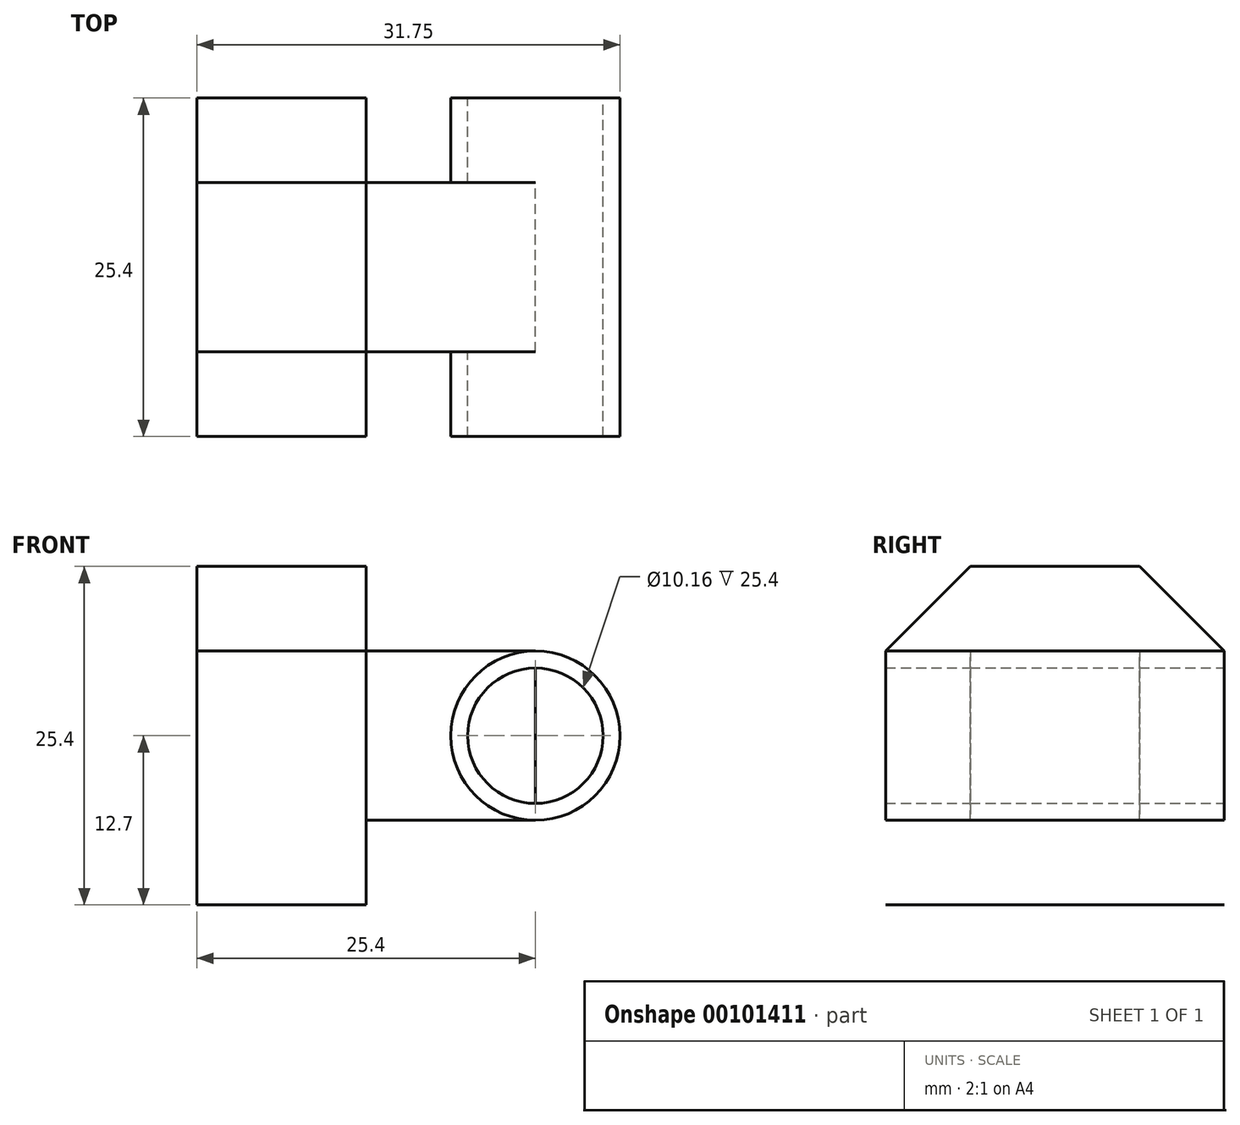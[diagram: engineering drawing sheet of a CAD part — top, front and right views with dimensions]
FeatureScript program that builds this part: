
annotation { "Feature Type Name" : "Feature", "Feature Type Description" : "" }
export const myFeature = defineFeature(function(context is Context, id is Id, definition is map)
    precondition{}
    {
        {
            var Q0;
            Q0=qCreatedBy(makeId("Right.planeOp"),FACE);
            var sketch = newSketch(context, id + "F0", { "sketchPlane" : qUnion([Q0])});
            skLineSegment(sketch, "E0", {"start": v(0, 0) * mm, "end": v(0, 25.4) * mm});
            skLineSegment(sketch, "E1", {"start": v(0, 25.4) * mm, "end": v(6.35, 25.4) * mm});
            skLineSegment(sketch, "E2", {"start": v(6.35, 25.4) * mm, "end": v(12.7, 19.05) * mm});
            skLineSegment(sketch, "E3", {"start": v(12.7, 19.05) * mm, "end": v(12.7, 0) * mm});
            skLineSegment(sketch, "E4", {"start": v(12.7, 0) * mm, "end": v(0, 0) * mm});
            skLineSegment(sketch, "E5.MirrorCS", {"start": v(0, 25.4) * mm, "end": v(-6.35, 25.4) * mm});
            skLineSegment(sketch, "E6.MirrorCS", {"start": v(-12.7, 0) * mm, "end": v(0, 0) * mm});
            skLineSegment(sketch, "E7.MirrorCS", {"start": v(-6.35, 25.4) * mm, "end": v(-12.7, 19.05) * mm});
            skLineSegment(sketch, "E8.MirrorCS", {"start": v(-12.7, 19.05) * mm, "end": v(-12.7, 0) * mm});
            skLineSegment(sketch, "E9", {"start": v(0, 19.05) * mm, "end": v(6.35, 19.05) * mm});
            skLineSegment(sketch, "E10", {"start": v(6.35, 19.05) * mm, "end": v(6.35, 6.35) * mm});
            skLineSegment(sketch, "E11", {"start": v(6.35, 6.35) * mm, "end": v(-6.35, 6.35) * mm});
            skLineSegment(sketch, "E12", {"start": v(-6.35, 6.35) * mm, "end": v(-6.35, 19.05) * mm});
            skLineSegment(sketch, "E13", {"start": v(-6.35, 19.05) * mm, "end": v(0, 19.05) * mm});
            skSolve(sketch);
        }
        {
            var Q0;
            {var subQ2=sQuery(id+"F0.wireOp",EDGE,"E5.MirrorCS");Q0=makeQuery(id+"F0.imprint","IMPRINT",FACE,{"disambiguationData":[TD([[makeQuery(id+"F0.imprint","IMPRINT",EDGE,{"derivedFrom":subQ2}),1.0]])]});}
            var Q1;
            {var subQ1=sQuery(id+"F0.wireOp",EDGE,"E1");Q1=makeQuery(id+"F0.imprint","IMPRINT",FACE,{"disambiguationData":[TD([[makeQuery(id+"F0.imprint","IMPRINT",EDGE,{"derivedFrom":subQ1}),-1.0]])]});}
            extrude(context, id + "F1", {"entities" : qUnion([Q0, Q1]), "depth" : 12.7 * mm});
        }
        {
            var Q0;
            {var subQ0=sQuery(id+"F0.wireOp",EDGE,"E9");Q0=makeQuery(id+"F0.imprint","IMPRINT",FACE,{"disambiguationData":[TD([[makeQuery(id+"F0.imprint","IMPRINT",EDGE,{"derivedFrom":subQ0}),-1.0]])]});}
            var Q1;
            {var subQ4=sQuery(id+"F0.wireOp",EDGE,"E12");Q1=makeQuery(id+"F0.imprint","IMPRINT",FACE,{"disambiguationData":[TD([[makeQuery(id+"F0.imprint","IMPRINT",EDGE,{"derivedFrom":subQ4}),-1.0]])]});}
            extrude(context, id + "F2", {"entities" : qUnion([Q0, Q1]), "operationType" : NewBodyOperationType.ADD, "depth" : 25.4 * mm});
        }
        {
            var Q0;
            Q0=makeQuery(id+"F2.opExtrude","SWEPT_FACE",FACE,{"disambiguationData":[OSD([sQuery(id+"F0.wireOp",EDGE,"E12")])]});
            var sketch = newSketch(context, id + "F3", { "sketchPlane" : qUnion([Q0])});
            skCircle(sketch, "E14", {"center": v(25.4, 12.7) * mm, "radius": 6.35 * mm});
            skCircle(sketch, "E15", {"center": v(25.4, 12.7) * mm, "radius": 5.08 * mm});
            skSolve(sketch);
        }
        {
            var Q0;
            Q0 = qSketchRegion(id + "F3", true);
            extrude(context, id + "F4", {"entities" : qUnion([Q0]), "operationType" : NewBodyOperationType.ADD, "depth" : 6.35 * mm, "hasSecondDirection" : true, "secondDirectionOppositeDirection" : true, "secondDirectionDepth" : 19.05 * mm});
        }
    });
